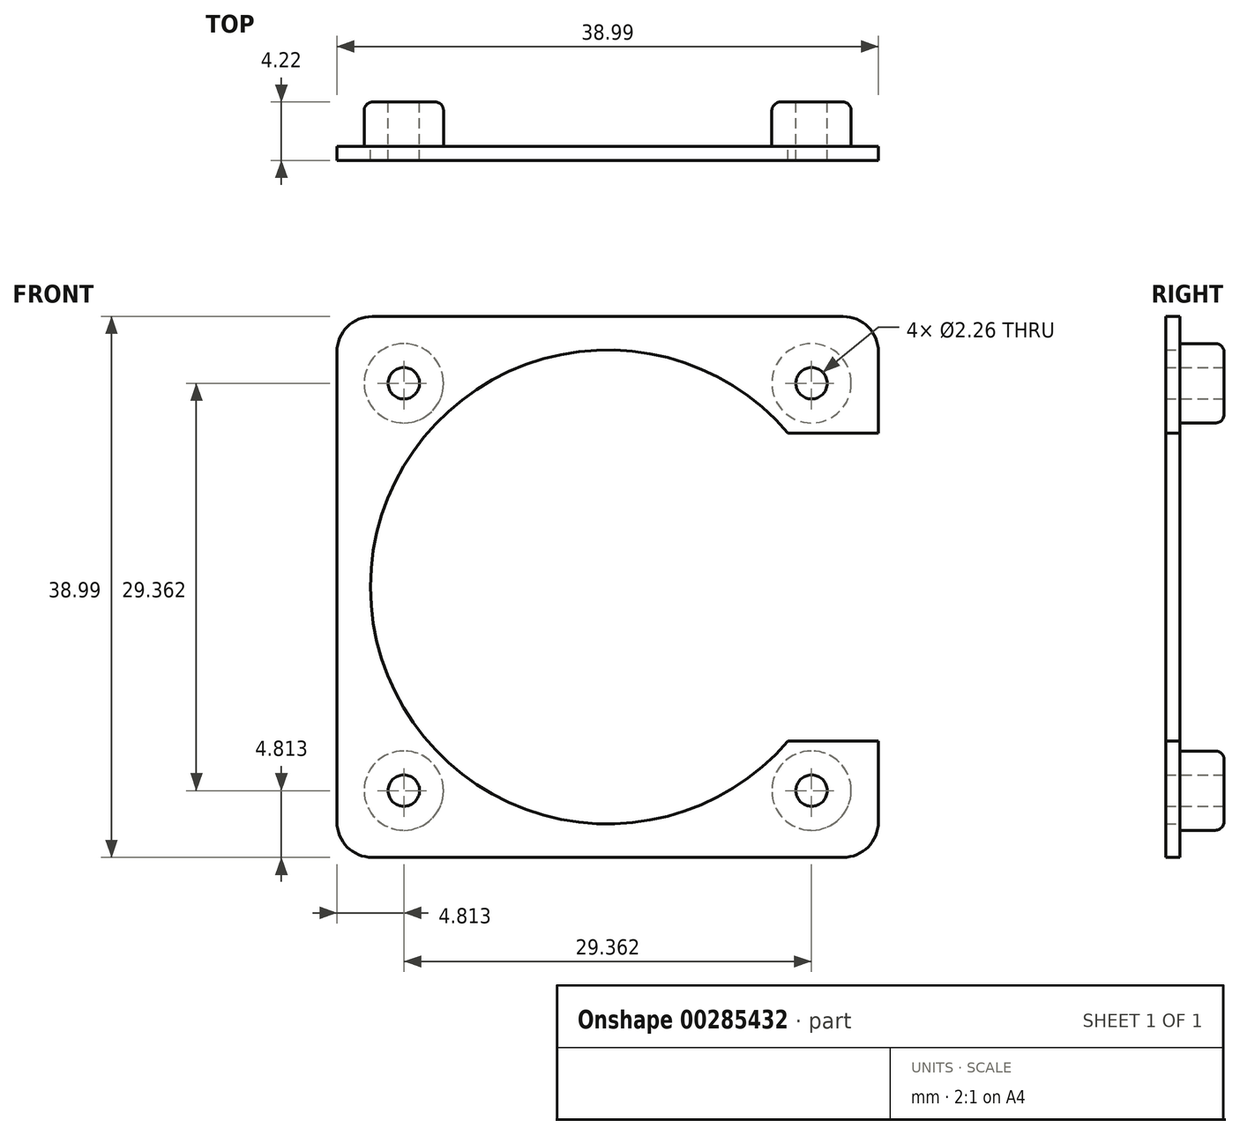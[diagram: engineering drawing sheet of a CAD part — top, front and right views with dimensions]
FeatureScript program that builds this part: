
annotation { "Feature Type Name" : "Feature", "Feature Type Description" : "" }
export const myFeature = defineFeature(function(context is Context, id is Id, definition is map)
    precondition{}
    {
        {
            var Q0;
            Q0=qCreatedBy(makeId("Front.planeOp"),FACE);
            var sketch = newSketch(context, id + "F0", { "sketchPlane" : qUnion([Q0])});
            skLineSegment(sketch, "E0.bottom", {"start": v(2.54, 0) * mm, "end": v(36.45, 0) * mm});
            skLineSegment(sketch, "E0.top", {"start": v(2.54, 38.99) * mm, "end": v(36.45, 38.99) * mm});
            skLineSegment(sketch, "E0.left", {"start": v(0, 2.54) * mm, "end": v(0, 36.45) * mm});
            skLineSegment(sketch, "E0.right", {"start": v(38.99, 2.54) * mm, "end": v(38.99, 8.4) * mm});
            skLineSegment(sketch, "E1", {"start": v(38.99, 30.6) * mm, "end": v(32.48, 30.6) * mm});
            skLineSegment(sketch, "E2", {"start": v(38.99, 8.4) * mm, "end": v(32.48, 8.4) * mm});
            skLineSegment(sketch, "E3", {"start": v(19.5, 38.99) * mm, "end": v(19.5, 0) * mm, "construction": true});
            skLineSegment(sketch, "E4", {"start": v(0, 19.5) * mm, "end": v(38.99, 19.5) * mm, "construction": true});
            skLineSegment(sketch, "E5", {"start": v(32.48, 30.6) * mm, "end": v(32.48, 8.4) * mm, "construction": true});
            skPoint(sketch, "E6", {"position": v(32.48, 19.5) * mm});
            skArc(sketch, "E7", {"start": v(32.48, 30.6) * mm, "mid": v(2.41, 19.5) * mm, "end": v(32.48, 8.4) * mm});
            skLineSegment(sketch, "E8.trimOffspring", {"start": v(38.99, 30.6) * mm, "end": v(38.99, 36.45) * mm});
            skPoint(sketch, "E9.visualSharp", {"position": v(0, 38.99) * mm});
            skArc(sketch, "E9.filletArc", {"start": v(2.54, 38.99) * mm, "mid": v(0.74, 38.25) * mm, "end": v(0, 36.45) * mm});
            skPoint(sketch, "E10.visualSharp", {"position": v(38.99, 38.99) * mm});
            skArc(sketch, "E10.filletArc", {"start": v(38.99, 36.45) * mm, "mid": v(38.25, 38.25) * mm, "end": v(36.45, 38.99) * mm});
            skPoint(sketch, "E11.visualSharp", {"position": v(38.99, 0) * mm});
            skArc(sketch, "E11.filletArc", {"start": v(36.45, 0) * mm, "mid": v(38.25, 0.74) * mm, "end": v(38.99, 2.54) * mm});
            skPoint(sketch, "E12.visualSharp", {"position": v(0, 0) * mm});
            skArc(sketch, "E12.filletArc", {"start": v(0, 2.54) * mm, "mid": v(0.74, 0.74) * mm, "end": v(2.54, 0) * mm});
            skSolve(sketch);
        }
        {
            var Q0;
            Q0 = qSketchRegion(id + "F0", true);
            extrude(context, id + "F1", {"entities" : qUnion([Q0]), "depth" : 1.02 * mm});
        }
        {
            var Q0;
            Q0=makeQuery(id+"F1.opExtrude","CAP_FACE",FACE,{"disambiguationData":[OSD([sQuery(id+"F0.wireOp",EDGE,"E0.bottom"),sQuery(id+"F0.wireOp",EDGE,"E0.top"),sQuery(id+"F0.wireOp",EDGE,"E0.left"),sQuery(id+"F0.wireOp",EDGE,"E0.right"),sQuery(id+"F0.wireOp",EDGE,"E1"),sQuery(id+"F0.wireOp",EDGE,"E2"),sQuery(id+"F0.wireOp",EDGE,"E7"),sQuery(id+"F0.wireOp",EDGE,"E8.trimOffspring"),sQuery(id+"F0.wireOp",EDGE,"E9.filletArc"),sQuery(id+"F0.wireOp",EDGE,"E10.filletArc"),sQuery(id+"F0.wireOp",EDGE,"E11.filletArc"),sQuery(id+"F0.wireOp",EDGE,"E12.filletArc")])],"isStart":true});
            var sketch = newSketch(context, id + "F2", { "sketchPlane" : qUnion([Q0])});
            skLineSegment(sketch, "E13.bottom", {"start": v(-34.18, 34.18) * mm, "end": v(-4.81, 34.18) * mm, "construction": true});
            skLineSegment(sketch, "E13.top", {"start": v(-34.18, 4.81) * mm, "end": v(-4.81, 4.81) * mm, "construction": true});
            skLineSegment(sketch, "E13.left", {"start": v(-34.18, 34.18) * mm, "end": v(-34.18, 4.81) * mm, "construction": true});
            skLineSegment(sketch, "E13.right", {"start": v(-4.81, 34.18) * mm, "end": v(-4.81, 4.81) * mm, "construction": true});
            skLineSegment(sketch, "E14", {"start": v(0, 19.5) * mm, "end": v(-34.18, 19.5) * mm, "construction": true});
            skPoint(sketch, "E14.endSnap0", {"position": v(-2.41, 19.5) * mm});
            skLineSegment(sketch, "E15", {"start": v(-19.5, 38.99) * mm, "end": v(-19.5, 4.81) * mm, "construction": true});
            skCircle(sketch, "E16", {"center": v(-34.18, 34.18) * mm, "radius": 2.86 * mm});
            skCircle(sketch, "E17", {"center": v(-4.81, 34.18) * mm, "radius": 2.86 * mm});
            skCircle(sketch, "E18", {"center": v(-4.81, 4.81) * mm, "radius": 2.86 * mm});
            skCircle(sketch, "E19", {"center": v(-34.18, 4.81) * mm, "radius": 2.86 * mm});
            skSolve(sketch);
        }
        {
            var Q0;
            Q0 = qSketchRegion(id + "F2", true);
            extrude(context, id + "F3", {"entities" : qUnion([Q0]), "operationType" : NewBodyOperationType.ADD, "depth" : 3.2 * mm});
        }
        {
            var Q0;
            Q0=makeQuery(id+"F3.opExtrude","CAP_FACE",FACE,{"disambiguationData":[OSD([sQuery(id+"F2.wireOp",EDGE,"E16")])],"isStart":false});
            var sketch = newSketch(context, id + "F4", { "sketchPlane" : qUnion([Q0])});
            skPoint(sketch, "E20", {"position": v(-34.18, 34.18) * mm});
            skPoint(sketch, "E21", {"position": v(-4.81, 34.18) * mm});
            skPoint(sketch, "E22", {"position": v(-4.81, 4.81) * mm});
            skPoint(sketch, "E23", {"position": v(-34.18, 4.81) * mm});
            skSolve(sketch);
        }
        {
            var Q0;
            Q0=sQuery(id+"F4.wireOp",VERTEX,"E20");
            var Q1;
            Q1=sQuery(id+"F4.wireOp",VERTEX,"E22");
            var Q2;
            Q2=sQuery(id+"F4.wireOp",VERTEX,"E23");
            var Q3;
            Q3=sQuery(id+"F4.wireOp",VERTEX,"E21");
            var Q4;
            Q4=makeQuery(id+"F1.opExtrude","SWEPT_BODY",BODY,{"disambiguationData":[OSD([sQuery(id+"F0.wireOp",EDGE,"E0.bottom"),sQuery(id+"F0.wireOp",EDGE,"E0.top"),sQuery(id+"F0.wireOp",EDGE,"E0.left"),sQuery(id+"F0.wireOp",EDGE,"E0.right"),sQuery(id+"F0.wireOp",EDGE,"E1"),sQuery(id+"F0.wireOp",EDGE,"E2"),sQuery(id+"F0.wireOp",EDGE,"E7"),sQuery(id+"F0.wireOp",EDGE,"E8.trimOffspring"),sQuery(id+"F0.wireOp",EDGE,"E9.filletArc"),sQuery(id+"F0.wireOp",EDGE,"E10.filletArc"),sQuery(id+"F0.wireOp",EDGE,"E11.filletArc"),sQuery(id+"F0.wireOp",EDGE,"E12.filletArc")])]});
            hole(context, id + "F5", {"style" : HoleStyle.SIMPLE, "endStyle" : HoleEndStyle.THROUGH, "standardTappedOrClearance" : lookupTablePath({ "standard" : "ANSI", "engagement" : "75%", "pitch" : "40 tpi", "size" : "#4", "type" : "Tapped" }), "standardBlindInLast" : lookupTablePath({ "standard" : "ANSI", "engagement" : "75%", "pitch" : "40 tpi", "size" : "#4", "type" : "Tapped" }), "holeDiameter" : 2.26 * mm, "showTappedDepth" : true, "isTappedThrough" : true, "tappedDepth" : 2.4 * mm, "tapClearance" : 3, "startFromSketch" : true, "locations" : qUnion([Q0, Q1, Q2, Q3]), "scope" : qUnion([Q4]), "majorDiameter" : 2.84 * mm});
        }
        {
            var Q0;
            Q0=makeQuery(id+"F3.opExtrude","CAP_EDGE",EDGE,{"disambiguationData":[OSD([sQuery(id+"F2.wireOp",EDGE,"E16")])],"isStart":false});
            var Q1;
            Q1=makeQuery(id+"F3.opExtrude","CAP_EDGE",EDGE,{"disambiguationData":[OSD([sQuery(id+"F2.wireOp",EDGE,"E17")])],"isStart":false});
            var Q2;
            Q2=makeQuery(id+"F3.opExtrude","CAP_EDGE",EDGE,{"disambiguationData":[OSD([sQuery(id+"F2.wireOp",EDGE,"E18")])],"isStart":false});
            var Q3;
            Q3=makeQuery(id+"F3.opExtrude","CAP_EDGE",EDGE,{"disambiguationData":[OSD([sQuery(id+"F2.wireOp",EDGE,"E19")])],"isStart":false});
            fillet(context, id + "F6", {"entities" : qUnion([Q0, Q1, Q2, Q3]), "radius" : 0.64 * mm, "tangentPropagation" : true, "allowEdgeOverflow" : false});
        }
    });
